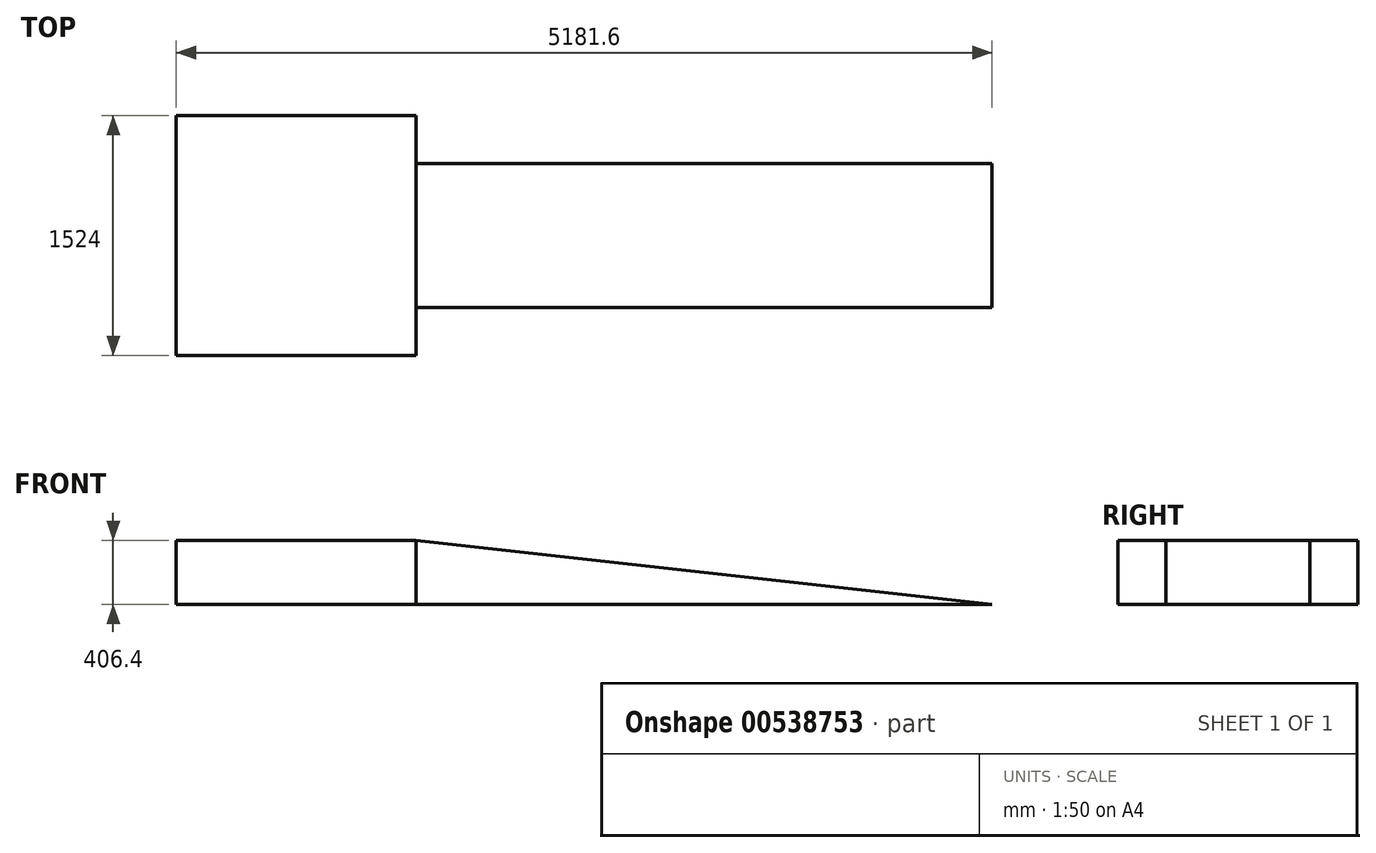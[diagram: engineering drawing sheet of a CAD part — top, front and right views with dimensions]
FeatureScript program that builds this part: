
annotation { "Feature Type Name" : "Feature", "Feature Type Description" : "" }
export const myFeature = defineFeature(function(context is Context, id is Id, definition is map)
    precondition{}
    {
        {
            var Q0;
            Q0=qCreatedBy(makeId("Front.planeOp"),FACE);
            var sketch = newSketch(context, id + "F0", { "sketchPlane" : qUnion([Q0])});
            skLineSegment(sketch, "E0.bottom", {"start": v(-762, 203.2) * mm, "end": v(762, 203.2) * mm});
            skLineSegment(sketch, "E0.top", {"start": v(-762, -203.2) * mm, "end": v(762, -203.2) * mm});
            skLineSegment(sketch, "E0.left", {"start": v(-762, 203.2) * mm, "end": v(-762, -203.2) * mm});
            skLineSegment(sketch, "E0.right", {"start": v(762, 203.2) * mm, "end": v(762, -203.2) * mm});
            skPoint(sketch, "E0.middle", {"position": v(0, 0) * mm});
            skLineSegment(sketch, "E1", {"start": v(762, -203.2) * mm, "end": v(4419.6, -203.2) * mm});
            skLineSegment(sketch, "E2", {"start": v(4419.6, -203.2) * mm, "end": v(762, 203.2) * mm});
            skSolve(sketch);
        }
        {
            var Q0;
            Q0=makeQuery(id+"F0.imprint","IMPRINT",FACE,{"disambiguationData":[TD([[makeQuery(id+"F0.imprint","IMPRINT",EDGE,{"derivedFrom":sQuery(id+"F0.wireOp",EDGE,"E0.bottom")}),-1.0]])]});
            extrude(context, id + "F1", {"entities" : qUnion([Q0]), "endBound" : BoundingType.SYMMETRIC, "depth" : 1524 * mm, "offsetDistance" : 25.4 * mm});
        }
        {
            var Q0;
            Q0 = qSketchRegion(id + "F0", true);
            extrude(context, id + "F2", {"entities" : qUnion([Q0]), "operationType" : NewBodyOperationType.ADD, "endBound" : BoundingType.SYMMETRIC, "depth" : 914.4 * mm, "offsetDistance" : 25.4 * mm});
        }
    });
